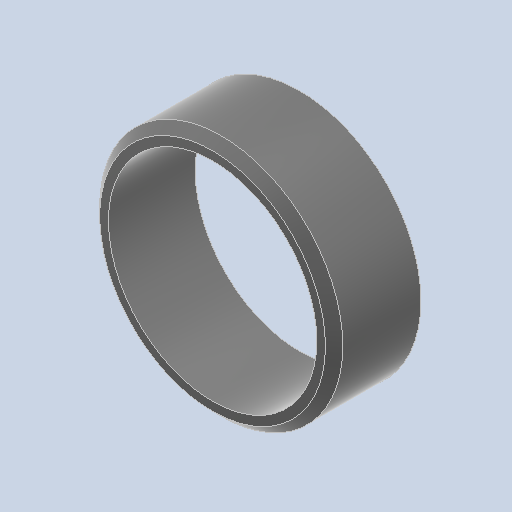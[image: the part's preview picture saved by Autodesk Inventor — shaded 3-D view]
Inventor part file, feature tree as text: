
AUTODESK INVENTOR PART (.ipt)
format: ipt  version: 2023 (Build 270158000, 158)  size: 112,640 bytes
history: native  units: mm
features: other x3, sketch x1
ambient origin geometry x8: Origin, YZ Plane, XZ Plane, XY Plane, X Axis, Y Axis, Z Axis, Center Point
bodies: Solid1 (feature_tree)
feature tree (4):
  other  "w5f12-14n.ipt"
  other  "Solid1::w5f12-14n.ipt"
  other  "TaggingFeature1"
  sketch  "Sketch1"  dims[d0=10.0mm]
